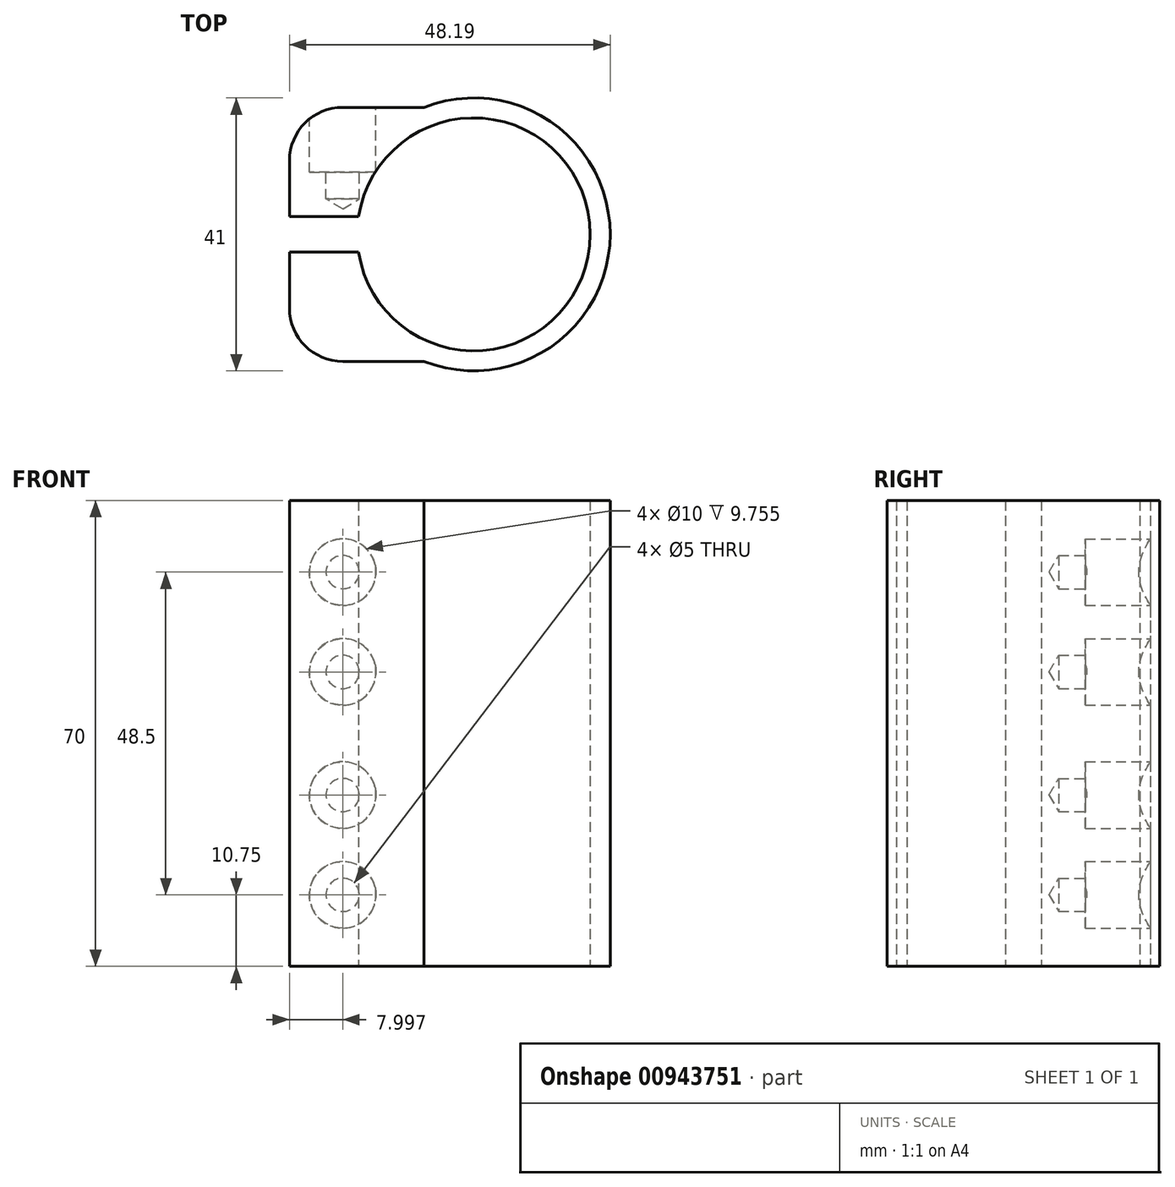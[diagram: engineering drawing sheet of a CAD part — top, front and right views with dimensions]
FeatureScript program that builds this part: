
annotation { "Feature Type Name" : "Feature", "Feature Type Description" : "" }
export const myFeature = defineFeature(function(context is Context, id is Id, definition is map)
    precondition{}
    {
        {
            var Q0;
            Q0=qCreatedBy(makeId("Top.planeOp"),FACE);
            var sketch = newSketch(context, id + "F0", { "sketchPlane" : qUnion([Q0])});
            skArc(sketch, "E0", {"start": v(-17.3, -2.68) * mm, "mid": v(17.5, 0) * mm, "end": v(-17.3, 2.68) * mm});
            skArc(sketch, "E1", {"start": v(-7.5, -19.08) * mm, "mid": v(20.5, 0) * mm, "end": v(-7.5, 19.08) * mm});
            skLineSegment(sketch, "E2", {"start": v(-7.5, 19.08) * mm, "end": v(-19.7, 19.08) * mm});
            skLineSegment(sketch, "E3", {"start": v(-27.7, 11.08) * mm, "end": v(-27.7, 2.68) * mm});
            skLineSegment(sketch, "E4", {"start": v(-27.7, 2.68) * mm, "end": v(-17.3, 2.68) * mm});
            skPoint(sketch, "E5.visualSharp", {"position": v(-27.7, 19.08) * mm});
            skArc(sketch, "E5.filletArc", {"start": v(-19.7, 19.08) * mm, "mid": v(-25.35, 16.74) * mm, "end": v(-27.7, 11.08) * mm});
            skLineSegment(sketch, "E6.MirrorCS", {"start": v(-7.5, -19.08) * mm, "end": v(-19.7, -19.08) * mm});
            skArc(sketch, "E7.MirrorCS", {"start": v(-19.7, -19.08) * mm, "mid": v(-25.35, -16.74) * mm, "end": v(-27.7, -11.08) * mm});
            skLineSegment(sketch, "E8.MirrorCS", {"start": v(-27.7, -2.68) * mm, "end": v(-17.3, -2.68) * mm});
            skLineSegment(sketch, "E9.MirrorCS", {"start": v(-27.7, -11.08) * mm, "end": v(-27.7, -2.68) * mm});
            skSolve(sketch);
        }
        {
            var Q0;
            Q0=makeQuery(id+"F0.imprint","IMPRINT",FACE,{"disambiguationData":[TD([[makeQuery(id+"F0.imprint","IMPRINT",EDGE,{"derivedFrom":sQuery(id+"F0.wireOp",EDGE,"E0")}),-1.0]])]});
            extrude(context, id + "F1", {"entities" : qUnion([Q0]), "endBound" : BoundingType.SYMMETRIC, "depth" : 70 * mm, "offsetDistance" : 25 * mm});
        }
        {
            var Q0;
            Q0=makeQuery(id+"F1.opExtrude","SWEPT_FACE",FACE,{"disambiguationData":[OSD([sQuery(id+"F0.wireOp",EDGE,"E2")])]});
            var sketch = newSketch(context, id + "F2", { "sketchPlane" : qUnion([Q0])});
            skPoint(sketch, "E10", {"position": v(19.7, 24.25) * mm});
            skPoint(sketch, "E11", {"position": v(19.7, 9.25) * mm});
            skPoint(sketch, "E12", {"position": v(19.7, -9.25) * mm});
            skPoint(sketch, "E13", {"position": v(19.7, -24.25) * mm});
            skPoint(sketch, "E14", {"position": v(0, -9.25) * mm});
            skSolve(sketch);
        }
        {
            var Q0;
            Q0=sQuery(id+"F2.wireOp",VERTEX,"E10");
            var Q1;
            Q1=sQuery(id+"F2.wireOp",VERTEX,"E11");
            var Q2;
            Q2=sQuery(id+"F2.wireOp",VERTEX,"E12");
            var Q3;
            Q3=sQuery(id+"F2.wireOp",VERTEX,"E13");
            var Q4;
            Q4=makeQuery(id+"F1.opExtrude","SWEPT_BODY",BODY,{"disambiguationData":[OSD([sQuery(id+"F0.wireOp",EDGE,"E0"),sQuery(id+"F0.wireOp",EDGE,"E1"),sQuery(id+"F0.wireOp",EDGE,"E2"),sQuery(id+"F0.wireOp",EDGE,"E3"),sQuery(id+"F0.wireOp",EDGE,"E4"),sQuery(id+"F0.wireOp",EDGE,"E5.filletArc"),sQuery(id+"F0.wireOp",EDGE,"E6.MirrorCS"),sQuery(id+"F0.wireOp",EDGE,"E7.MirrorCS"),sQuery(id+"F0.wireOp",EDGE,"E8.MirrorCS"),sQuery(id+"F0.wireOp",EDGE,"E9.MirrorCS")])]});
            hole(context, id + "F3", {"style" : HoleStyle.C_BORE, "endStyle" : HoleEndStyle.BLIND, "holeDiameter" : 5 * mm, "cBoreDiameter" : 10 * mm, "cBoreDepth" : 8 * mm, "majorDiameter" : 5 * mm, "holeDepth" : 12 * mm, "isTappedThrough" : true, "tappedDepth" : 12 * mm, "tapClearance" : 3, "locations" : qUnion([Q0, Q1, Q2, Q3]), "scope" : qUnion([Q4])});
        }
    });
